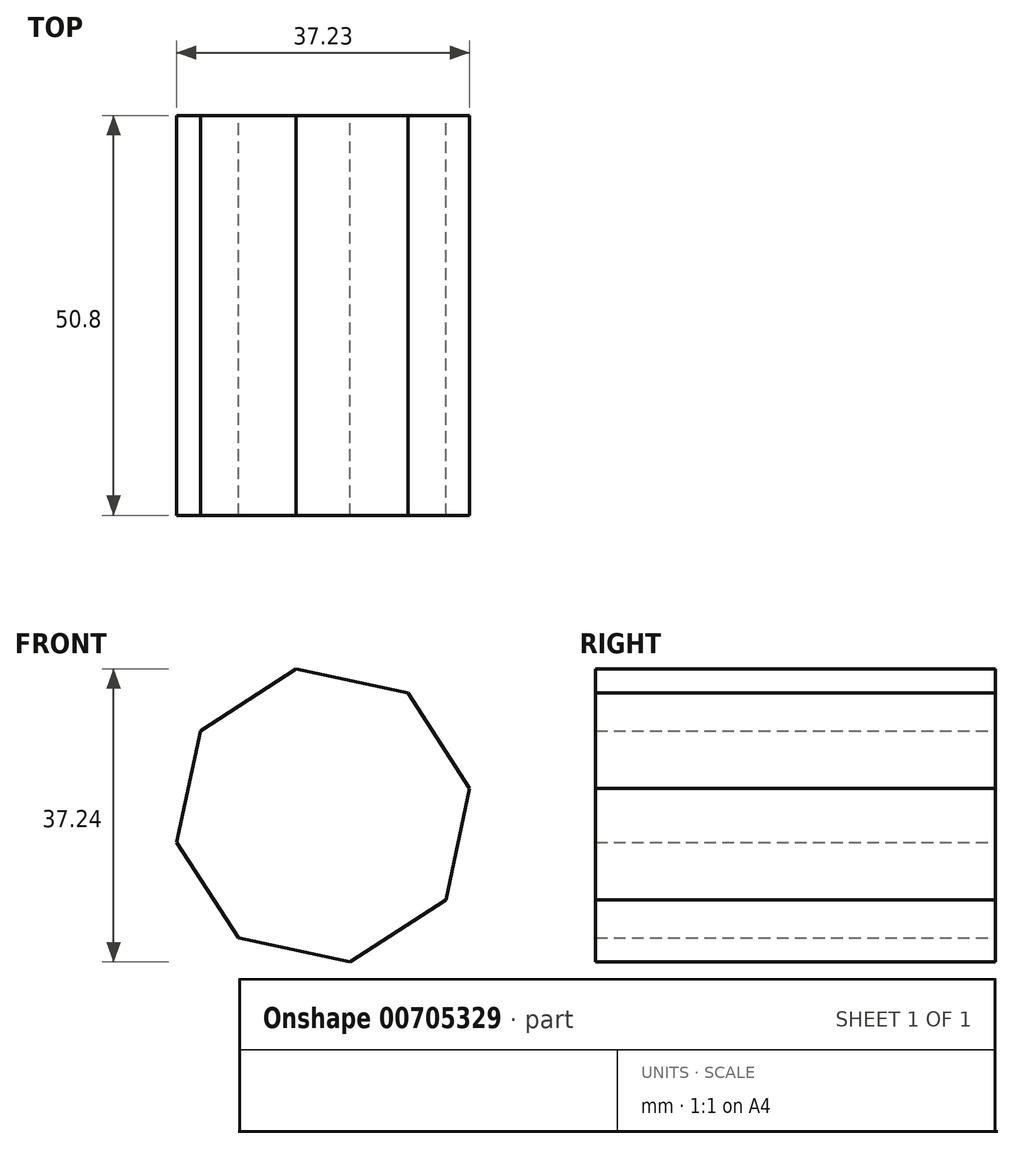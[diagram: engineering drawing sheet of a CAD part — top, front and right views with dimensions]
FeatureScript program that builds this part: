
annotation { "Feature Type Name" : "Feature", "Feature Type Description" : "" }
export const myFeature = defineFeature(function(context is Context, id is Id, definition is map)
    precondition{}
    {
        {
            var Q0;
            Q0=qCreatedBy(makeId("Front.planeOp"),FACE);
            var sketch = newSketch(context, id + "F0", { "sketchPlane" : qUnion([Q0])});
            skPoint(sketch, "E0.0.midPoint", {"position": v(-31.6, 46.27) * mm});
            skCircle(sketch, "E1.cCircle", {"center": v(-21.83, 16.64) * mm, "radius": 17.49 * mm, "construction": true});
            skLineSegment(sketch, "E1.0", {"start": v(-25.25, 35.26) * mm, "end": v(-11.09, 32.23) * mm});
            skLineSegment(sketch, "E1.1", {"start": v(-11.09, 32.23) * mm, "end": v(-3.22, 20.06) * mm});
            skLineSegment(sketch, "E1.2", {"start": v(-3.22, 20.06) * mm, "end": v(-6.25, 5.9) * mm});
            skLineSegment(sketch, "E1.3", {"start": v(-6.25, 5.9) * mm, "end": v(-18.42, -1.98) * mm});
            skLineSegment(sketch, "E1.4", {"start": v(-18.42, -1.98) * mm, "end": v(-32.58, 1.06) * mm});
            skLineSegment(sketch, "E1.5", {"start": v(-32.58, 1.06) * mm, "end": v(-40.45, 13.22) * mm});
            skLineSegment(sketch, "E1.6", {"start": v(-40.45, 13.22) * mm, "end": v(-37.42, 27.4) * mm});
            skLineSegment(sketch, "E1.7", {"start": v(-37.42, 27.4) * mm, "end": v(-25.25, 35.26) * mm});
            skPoint(sketch, "E1.0.midPoint", {"position": v(-18.17, 33.74) * mm});
            skPoint(sketch, "E0.1.start.orphan", {"position": v(-41.38, 30.7) * mm});
            skPoint(sketch, "E0.3.end.orphan", {"position": v(-21.83, 61.84) * mm});
            skSolve(sketch);
        }
        {
            var Q0;
            Q0=makeQuery(id+"F0.imprint","IMPRINT",FACE,{"disambiguationData":[TD([[makeQuery(id+"F0.imprint","IMPRINT",EDGE,{"derivedFrom":sQuery(id+"F0.wireOp",EDGE,"E1.0")}),-1.0]])]});
            extrude(context, id + "F1", {"entities" : qUnion([Q0]), "depth" : 25.4 * mm, "offsetDistance" : 25.4 * mm});
        }
        {
            var Q0;
            Q0=makeQuery(id+"F1.opExtrude","CAP_FACE",FACE,{"disambiguationData":[OSD([sQuery(id+"F0.wireOp",EDGE,"E1.0"),sQuery(id+"F0.wireOp",EDGE,"E1.1"),sQuery(id+"F0.wireOp",EDGE,"E1.2"),sQuery(id+"F0.wireOp",EDGE,"E1.3"),sQuery(id+"F0.wireOp",EDGE,"E1.4"),sQuery(id+"F0.wireOp",EDGE,"E1.5"),sQuery(id+"F0.wireOp",EDGE,"E1.6"),sQuery(id+"F0.wireOp",EDGE,"E1.7")])],"isStart":false});
            extrude(context, id + "F2", {"entities" : qUnion([Q0]), "operationType" : NewBodyOperationType.ADD, "depth" : 25.4 * mm, "offsetDistance" : 25.4 * mm});
        }
    });
